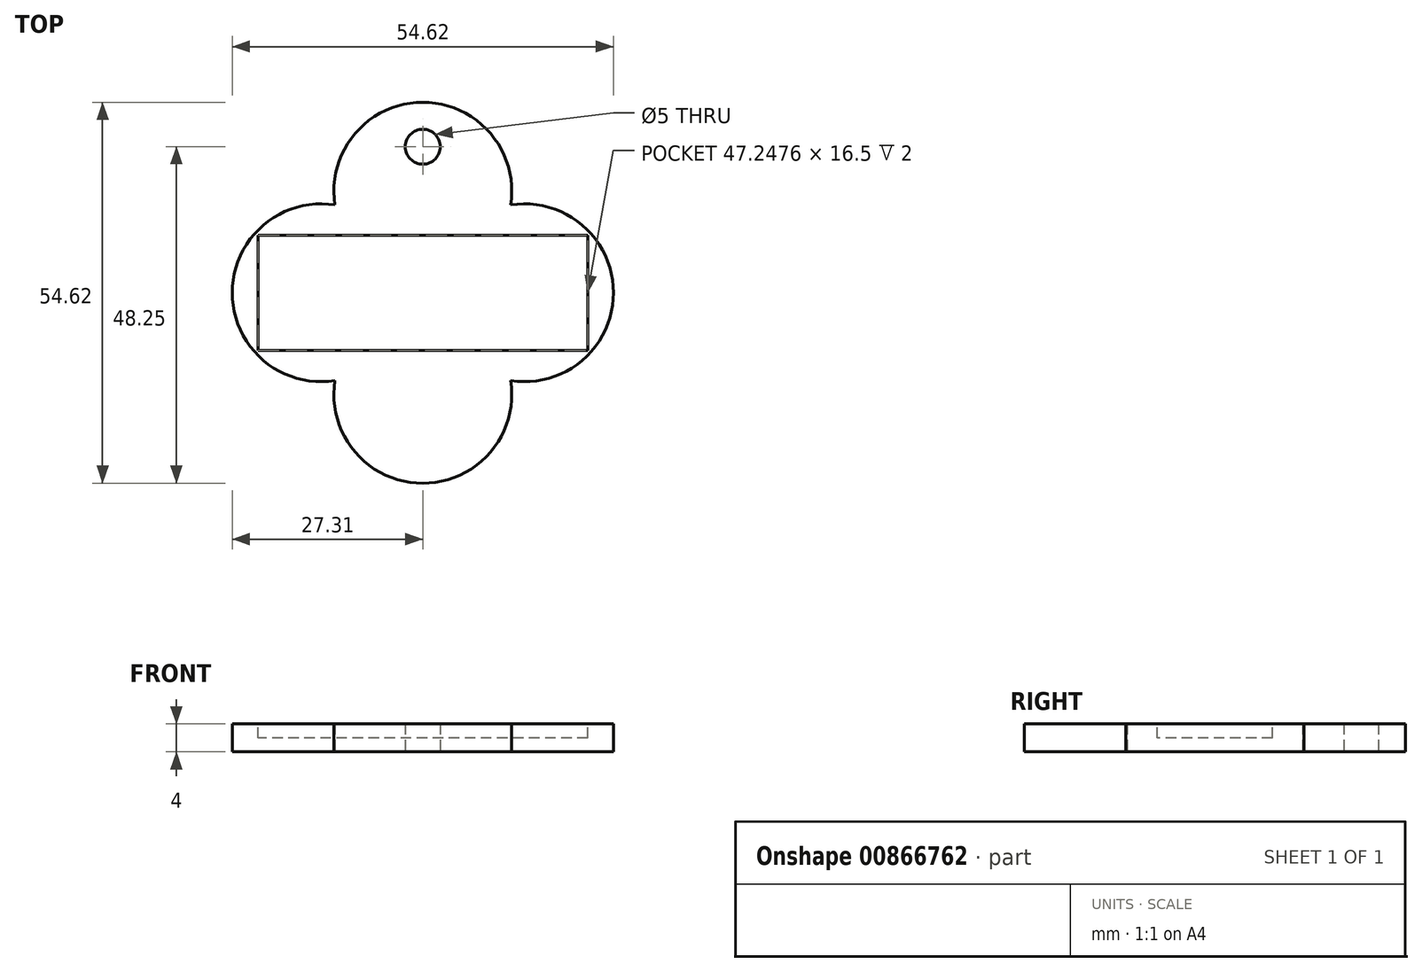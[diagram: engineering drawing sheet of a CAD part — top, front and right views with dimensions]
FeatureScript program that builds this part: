
annotation { "Feature Type Name" : "Feature", "Feature Type Description" : "" }
export const myFeature = defineFeature(function(context is Context, id is Id, definition is map)
    precondition{}
    {
        {
            var Q0;
            Q0=qCreatedBy(makeId("Top.planeOp"),FACE);
            var sketch = newSketch(context, id + "F0", { "sketchPlane" : qUnion([Q0])});
            skArc(sketch, "E0", {"start": v(-12.6, 12.6) * mm, "mid": v(-27.31, 0) * mm, "end": v(-12.6, -12.6) * mm});
            skArc(sketch, "E1.trimOffspring", {"start": v(12.6, 12.6) * mm, "mid": v(0, 27.31) * mm, "end": v(-12.6, 12.6) * mm});
            skArc(sketch, "E2.trimOffspring", {"start": v(12.6, -12.6) * mm, "mid": v(27.31, 0) * mm, "end": v(12.6, 12.6) * mm});
            skArc(sketch, "E3.trimOffspring", {"start": v(-12.6, -12.6) * mm, "mid": v(0, -27.31) * mm, "end": v(12.6, -12.6) * mm});
            skLineSegment(sketch, "E4", {"start": v(0, 14.57) * mm, "end": v(0, 27.31) * mm});
            skCircle(sketch, "E5", {"center": v(0, 20.94) * mm, "radius": 2.5 * mm});
            skSolve(sketch);
        }
        {
            var Q0;
            Q0=makeQuery(id+"F0.imprint","IMPRINT",FACE,{"disambiguationData":[TD([[makeQuery(id+"F0.imprint","IMPRINT",EDGE,{"derivedFrom":sQuery(id+"F0.wireOp",EDGE,"E0")}),1.0]])]});
            extrude(context, id + "F1", {"entities" : qUnion([Q0]), "depth" : 4 * mm, "offsetDistance" : 25 * mm});
        }
        {
            var Q0;
            Q0=makeQuery(id+"F1.opExtrude","CAP_FACE",FACE,{"disambiguationData":[OSD([sQuery(id+"F0.wireOp",EDGE,"E0"),sQuery(id+"F0.wireOp",EDGE,"E1.trimOffspring"),sQuery(id+"F0.wireOp",EDGE,"E2.trimOffspring"),sQuery(id+"F0.wireOp",EDGE,"E3.trimOffspring"),sQuery(id+"F0.wireOp",EDGE,"E5")])],"isStart":false});
            var sketch = newSketch(context, id + "F2", { "sketchPlane" : qUnion([Q0])});
            skLineSegment(sketch, "E6.bottom", {"start": v(23.62, 8.25) * mm, "end": v(-23.62, 8.25) * mm});
            skLineSegment(sketch, "E6.top", {"start": v(23.62, -8.25) * mm, "end": v(-23.62, -8.25) * mm});
            skLineSegment(sketch, "E6.left", {"start": v(23.62, 8.25) * mm, "end": v(23.62, -8.25) * mm});
            skLineSegment(sketch, "E6.right", {"start": v(-23.62, 8.25) * mm, "end": v(-23.62, -8.25) * mm});
            skPoint(sketch, "E6.middle", {"position": v(0, 0) * mm});
            skSolve(sketch);
        }
        {
            var Q0;
            Q0=makeQuery(id+"F2.imprint","IMPRINT",FACE,{"disambiguationData":[TD([[makeQuery(id+"F2.imprint","IMPRINT",EDGE,{"derivedFrom":sQuery(id+"F2.wireOp",EDGE,"E6.bottom")}),1.0]])]});
            extrude(context, id + "F3", {"entities" : qUnion([Q0]), "operationType" : NewBodyOperationType.REMOVE, "oppositeDirection" : true, "depth" : 2 * mm, "offsetDistance" : 25 * mm});
        }
    });
